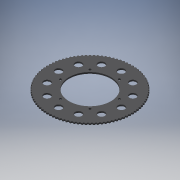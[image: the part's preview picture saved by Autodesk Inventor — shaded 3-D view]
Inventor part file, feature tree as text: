
AUTODESK INVENTOR PART (.ipt)
format: ipt  version: 2019.3 (Build 233278000, 278)  size: 329,728 bytes
history: native  units: mm
features: sketch x3, extrude x2, hole x2, pattern_circular x2
ambient origin geometry x8: Origin, YZ Plane, XZ Plane, XY Plane, X Axis, Y Axis, Z Axis, Center Point
bodies: Solid1 (feature_tree)
feature tree (9):
  extrude  "Extrusion1"  Depth=4.0mm TaperAngle=0.0deg
  sketch  "Sketch2"  dims[d3=19.0mm d4=120.0mm d6=360.0deg]
  extrude  "Extrusion2"  Depth=120.0mm TaperAngle=360.0deg
  hole  "Hole1"  [1 undecoded]
  pattern_circular  "Circular Pattern1"  Count=92 Angle=360.0deg
  hole  "Hole2"  [1 undecoded]
  pattern_circular  "Circular Pattern2"  Count=6 Angle=360.0deg
  sketch  "Sketch1"  dims[d0=233.0mm d1=4.0mm d2=0.0mm]
  sketch  "Sketch4"  dims[d8=116.0mm d9=0.0mm d11=116.0mm d12=5.0mm d13=6.0mm d14=4.0mm d15=2.0mm d16=90.0deg d17=8.0mm d18=20.594885mm d19=920.0mm d20=360.0deg d25=66.675mm d26=6.35mm d27=6.0mm d28=4.0mm d29=2.0mm d30=90.0deg d31=8.0mm d32=20.594885mm d33=60.0mm d34=360.0deg d36=87.0mm]
note: 2 required parameter values undecoded (feature->parameter linkage not recoverable at this tier; creation-order binding heuristic only, values carry confidence <= 0.55)
